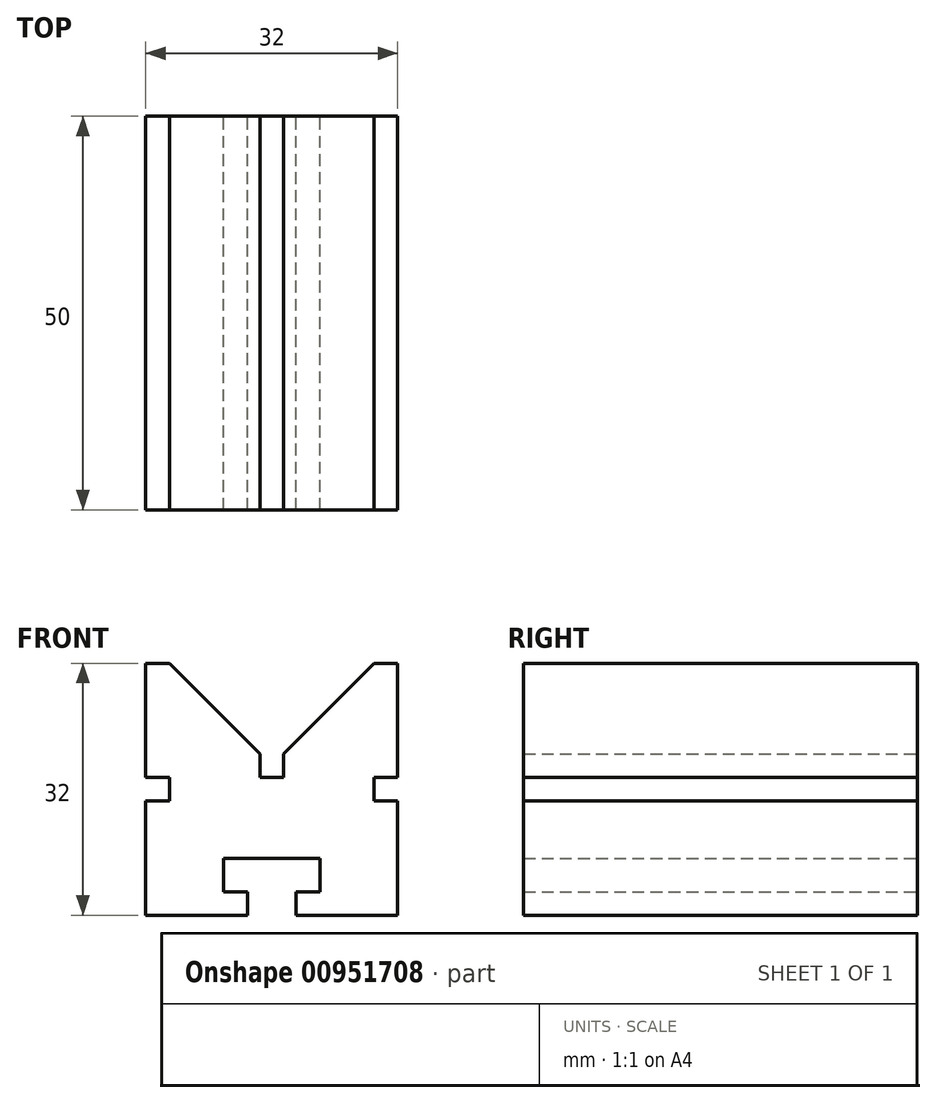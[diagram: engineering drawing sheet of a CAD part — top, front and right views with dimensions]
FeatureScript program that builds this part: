
annotation { "Feature Type Name" : "Feature", "Feature Type Description" : "" }
export const myFeature = defineFeature(function(context is Context, id is Id, definition is map)
    precondition{}
    {
        {
            var Q0;
            Q0=qCreatedBy(makeId("Front.planeOp"),FACE);
            var sketch = newSketch(context, id + "F0", { "sketchPlane" : qUnion([Q0])});
            skLineSegment(sketch, "E0", {"start": v(-16, -15.3) * mm, "end": v(-16, -0.8) * mm});
            skLineSegment(sketch, "E1", {"start": v(-16, -0.8) * mm, "end": v(-13, -0.8) * mm});
            skLineSegment(sketch, "E2", {"start": v(-13, -0.8) * mm, "end": v(-13, 2.2) * mm});
            skLineSegment(sketch, "E3", {"start": v(-13, 2.2) * mm, "end": v(-16, 2.2) * mm});
            skLineSegment(sketch, "E4", {"start": v(-16, 2.2) * mm, "end": v(-16, 16.7) * mm});
            skLineSegment(sketch, "E5", {"start": v(-16, 16.7) * mm, "end": v(-13, 16.7) * mm});
            skLineSegment(sketch, "E6", {"start": v(-16, -15.3) * mm, "end": v(-3.1, -15.3) * mm});
            skLineSegment(sketch, "E7", {"start": v(16, -15.3) * mm, "end": v(3.1, -15.3) * mm});
            skLineSegment(sketch, "E8", {"start": v(3.1, -15.3) * mm, "end": v(3.1, -12.3) * mm});
            skLineSegment(sketch, "E9", {"start": v(-3.1, -15.3) * mm, "end": v(-3.1, -12.3) * mm});
            skLineSegment(sketch, "E10", {"start": v(-3.1, -12.3) * mm, "end": v(-6.1, -12.3) * mm});
            skLineSegment(sketch, "E11", {"start": v(-6.1, -12.3) * mm, "end": v(-6.1, -8.1) * mm});
            skLineSegment(sketch, "E12", {"start": v(3.1, -12.3) * mm, "end": v(6.1, -12.3) * mm});
            skLineSegment(sketch, "E13", {"start": v(6.1, -12.3) * mm, "end": v(6.1, -8.1) * mm});
            skLineSegment(sketch, "E14", {"start": v(6.1, -8.1) * mm, "end": v(-6.1, -8.1) * mm});
            skLineSegment(sketch, "E15", {"start": v(16, -15.3) * mm, "end": v(16, -0.8) * mm});
            skLineSegment(sketch, "E16", {"start": v(16, 16.7) * mm, "end": v(16, 2.2) * mm});
            skLineSegment(sketch, "E17", {"start": v(16, 2.2) * mm, "end": v(13, 2.2) * mm});
            skLineSegment(sketch, "E18", {"start": v(13, 2.2) * mm, "end": v(13, -0.8) * mm});
            skLineSegment(sketch, "E19", {"start": v(13, -0.8) * mm, "end": v(16, -0.8) * mm});
            skLineSegment(sketch, "E20", {"start": v(16, 16.7) * mm, "end": v(13, 16.7) * mm});
            skLineSegment(sketch, "E21", {"start": v(0, 2.2) * mm, "end": v(1.5, 2.2) * mm});
            skLineSegment(sketch, "E22", {"start": v(0, 2.2) * mm, "end": v(-1.5, 2.2) * mm});
            skLineSegment(sketch, "E23", {"start": v(1.5, 2.2) * mm, "end": v(1.5, 5.2) * mm});
            skLineSegment(sketch, "E24", {"start": v(-1.5, 2.2) * mm, "end": v(-1.5, 5.2) * mm});
            skLineSegment(sketch, "E25", {"start": v(-1.5, 5.2) * mm, "end": v(-13, 16.7) * mm});
            skLineSegment(sketch, "E26", {"start": v(1.5, 5.2) * mm, "end": v(13, 16.7) * mm});
            skSolve(sketch);
        }
        {
            var Q0;
            Q0=makeQuery(id+"F0.imprint","IMPRINT",FACE,{"disambiguationData":[TD([[makeQuery(id+"F0.imprint","IMPRINT",EDGE,{"derivedFrom":sQuery(id+"F0.wireOp",EDGE,"E0")}),-1.0]])]});
            extrude(context, id + "F1", {"entities" : qUnion([Q0]), "depth" : 50 * mm, "offsetDistance" : 25 * mm, "symmetric" : true});
        }
    });
